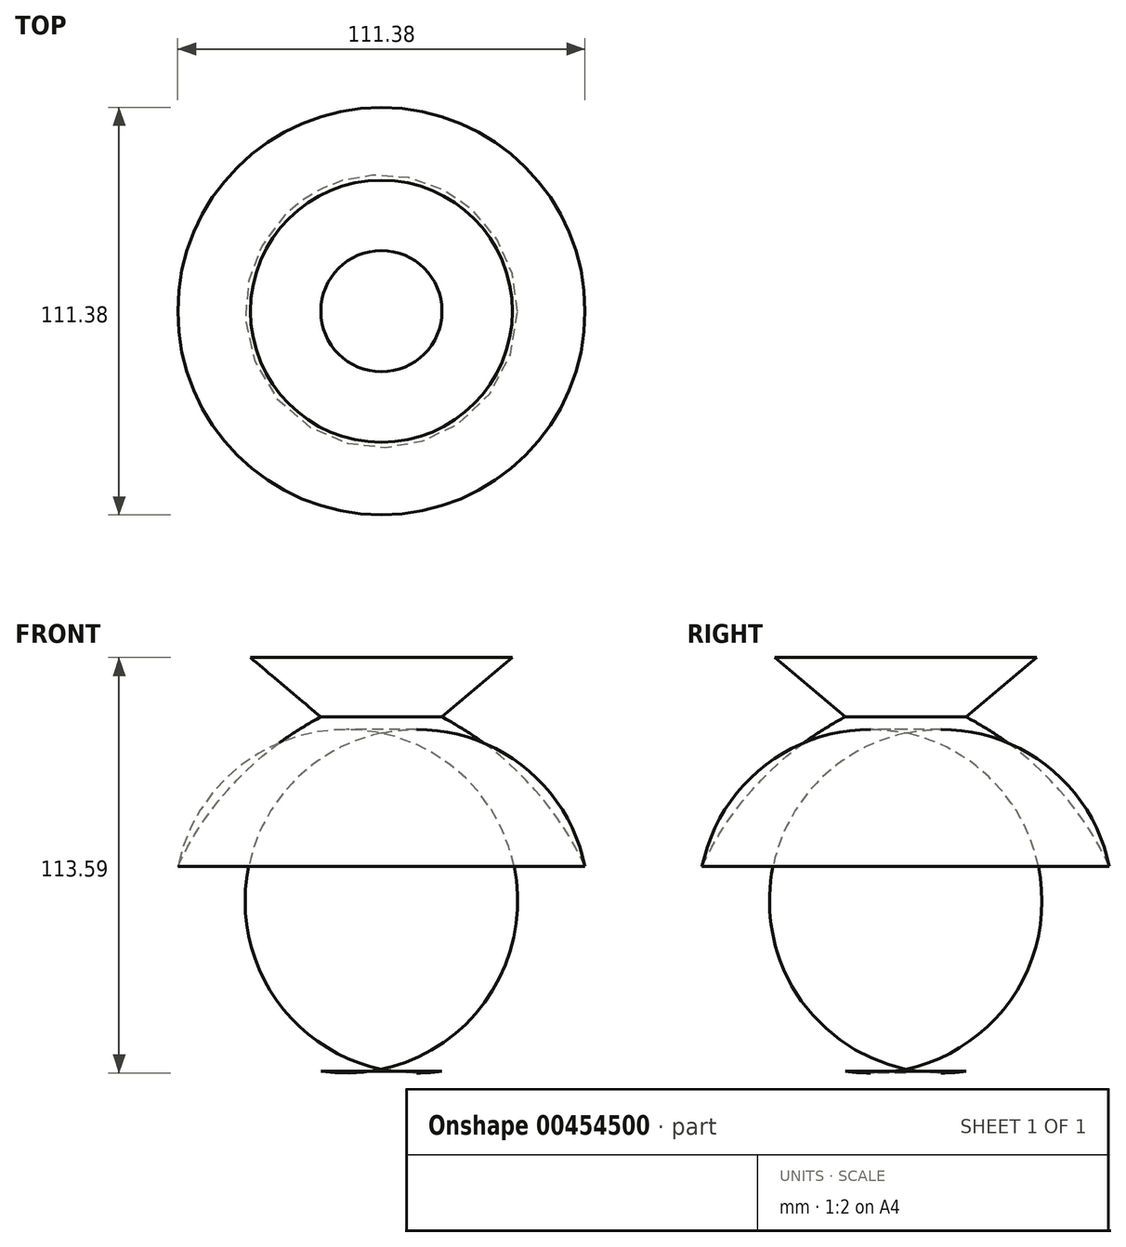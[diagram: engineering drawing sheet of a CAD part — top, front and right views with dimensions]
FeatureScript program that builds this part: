
annotation { "Feature Type Name" : "Feature", "Feature Type Description" : "" }
export const myFeature = defineFeature(function(context is Context, id is Id, definition is map)
    precondition{}
    {
        {
            var Q0;
            Q0=qCreatedBy(makeId("Front.planeOp"),FACE);
            var sketch = newSketch(context, id + "F0", { "sketchPlane" : qUnion([Q0])});
            skLineSegment(sketch, "E0", {"start": v(0, 57.11) * mm, "end": v(0, -59.11) * mm});
            skLineSegment(sketch, "E1", {"start": v(35.83, 57.11) * mm, "end": v(16.56, 40.84) * mm});
            skArc(sketch, "E2", {"start": v(55.69, 0) * mm, "mid": v(39.48, 23.63) * mm, "end": v(16.56, 40.84) * mm});
            skArc(sketch, "E3", {"start": v(16.56, -55.97) * mm, "mid": v(48.2, -36.42) * mm, "end": v(55.69, 0) * mm});
            skLineSegment(sketch, "E4", {"start": v(16.56, -55.97) * mm, "end": v(0, -55.97) * mm});
            skLineSegment(sketch, "E5", {"start": v(0, 57.11) * mm, "end": v(0, 57.11) * mm});
            skLineSegment(sketch, "E6", {"start": v(0, 57.11) * mm, "end": v(0, -55.97) * mm});
            skLineSegment(sketch, "E7", {"start": v(35.83, 57.11) * mm, "end": v(35.83, 58.33) * mm});
            skLineSegment(sketch, "E8", {"start": v(35.83, 58.33) * mm, "end": v(0, 57.11) * mm});
            skSolve(sketch);
        }
        {
            var Q0;
            Q0=sQuery(id+"F0.wireOp",EDGE,"oEJvp1jF-8tUr-oKBf-dVkm-6m057h8mHnsf");
            var Q1;
            Q1=sQuery(id+"F0.wireOp",EDGE,"E1");
            var Q2;
            Q2=sQuery(id+"F0.wireOp",EDGE,"E2");
            var Q3;
            Q3=sQuery(id+"F0.wireOp",EDGE,"E3");
            var Q4;
            Q4=sQuery(id+"F0.wireOp",EDGE,"E6");
            revolve(context, id + "F1", {"bodyType" : ToolBodyType.SURFACE, "surfaceEntities" : qUnion([Q0, Q1, Q2, Q3]), "axis" : qUnion([Q4]), "revolveType" : RevolveType.FULL});
        }
    });
